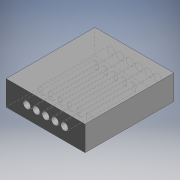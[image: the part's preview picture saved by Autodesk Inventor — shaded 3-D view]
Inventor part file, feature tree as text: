
AUTODESK INVENTOR PART (.ipt)
format: ipt  version: 2019 (Build 230136000, 136)  size: 129,024 bytes
history: native  units: mm (DEFAULTED — no unit token found)
features: sketch x2, hole x2, extrude x1
ambient origin geometry x8: Origin, YZ Plane, XZ Plane, XY Plane, X Axis, Y Axis, Z Axis, Center Point
bodies: Solid1 (feature_tree)
feature tree (5):
  sketch  "Sketch1"  dims[d0=0.0mm d1=57.15mm d2=57.15mm d3=0.0mm]
  sketch  "Sketch2"  dims[d4=4.7625mm d5=19.05mm d6=9.525mm d7=6.35mm d8=14.3117mm d9=44.499505mm d10=20.594885mm d11=4.7625mm d12=19.05mm d13=9.525mm d14=6.35mm d15=14.3117mm d16=44.499505mm d17=20.594885mm]
  extrude  "Extrusion1"  Depth=57.15mm TaperAngle=0.0deg
  hole  "Hole1"  [1 undecoded]
  hole  "Hole2"  [1 undecoded]
note: 2 required parameter values undecoded (feature->parameter linkage not recoverable at this tier; creation-order binding heuristic only, values carry confidence <= 0.55)
